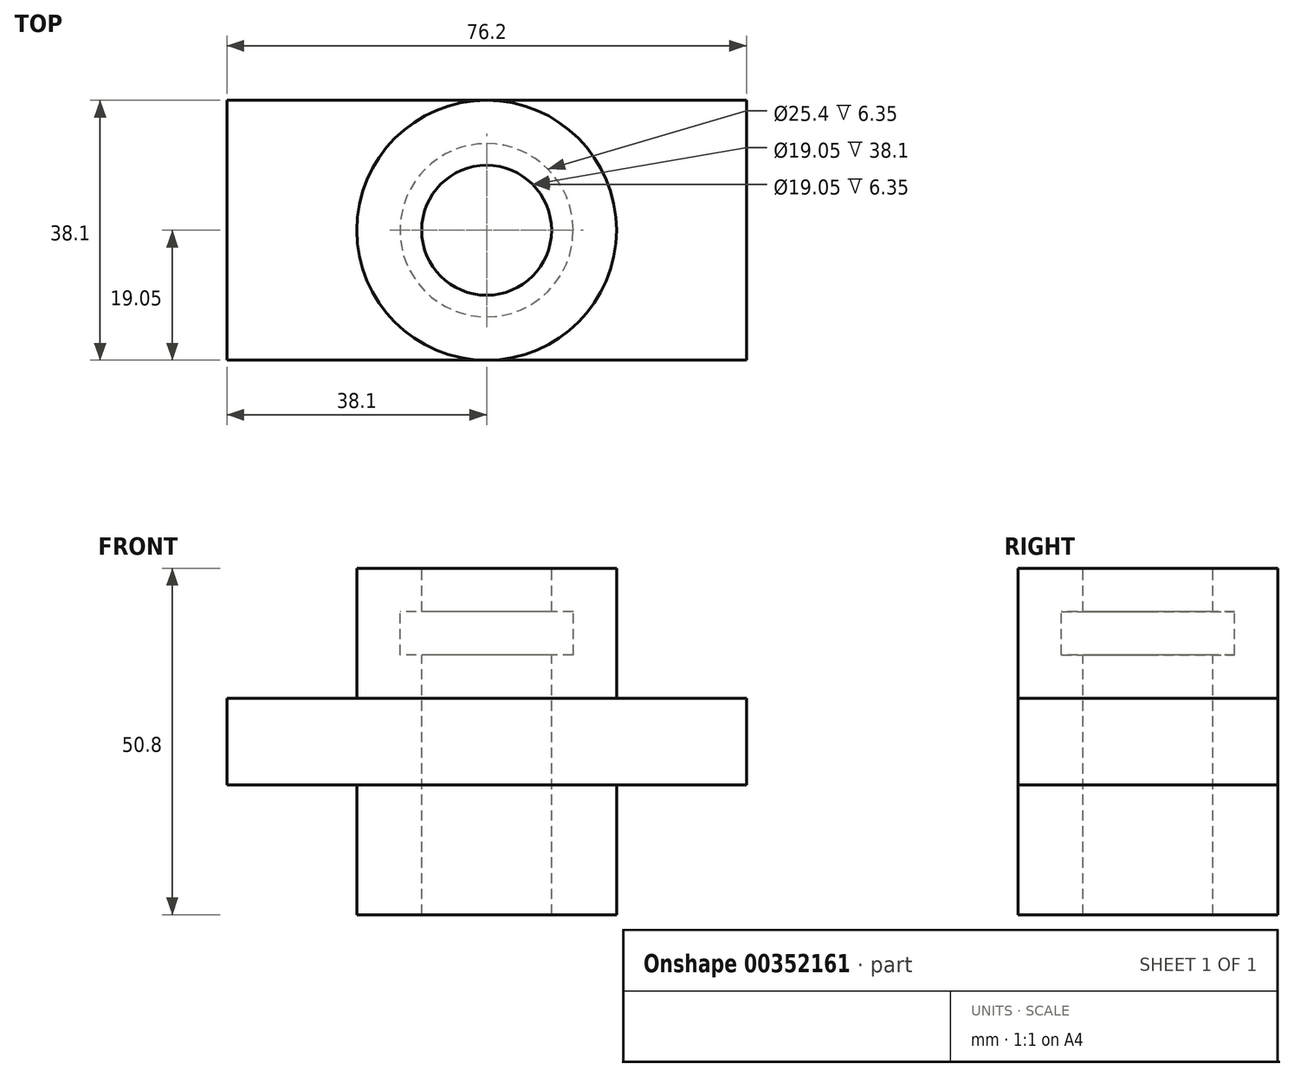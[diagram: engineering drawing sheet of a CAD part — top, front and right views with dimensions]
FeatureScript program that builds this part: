
annotation { "Feature Type Name" : "Feature", "Feature Type Description" : "" }
export const myFeature = defineFeature(function(context is Context, id is Id, definition is map)
    precondition{}
    {
        {
            var Q0;
            Q0=qCreatedBy(makeId("Top.planeOp"),FACE);
            var sketch = newSketch(context, id + "F0", { "sketchPlane" : qUnion([Q0])});
            skLineSegment(sketch, "E0", {"start": v(0, 0) * mm, "end": v(76.2, 0) * mm});
            skLineSegment(sketch, "E1", {"start": v(76.2, 0) * mm, "end": v(76.2, 38.1) * mm});
            skLineSegment(sketch, "E2", {"start": v(76.2, 38.1) * mm, "end": v(0, 38.1) * mm});
            skLineSegment(sketch, "E3", {"start": v(0, 38.1) * mm, "end": v(0, 0) * mm});
            skSolve(sketch);
        }
        {
            var Q0;
            Q0 = qSketchRegion(id + "F0", true);
            extrude(context, id + "F1", {"entities" : qUnion([Q0]), "endBound" : BoundingType.SYMMETRIC, "depth" : 12.7 * mm});
        }
        {
            var Q0;
            Q0=qCreatedBy(makeId("Top.planeOp"),FACE);
            var sketch = newSketch(context, id + "F2", { "sketchPlane" : qUnion([Q0])});
            skCircle(sketch, "E4", {"center": v(38.1, 19.05) * mm, "radius": 19.05 * mm});
            skSolve(sketch);
        }
        {
            var Q0;
            Q0 = qSketchRegion(id + "F2", true);
            extrude(context, id + "F3", {"entities" : qUnion([Q0]), "operationType" : NewBodyOperationType.ADD, "endBound" : BoundingType.SYMMETRIC, "depth" : 50.8 * mm});
        }
        {
            var Q0;
            Q0=makeQuery(id+"F3.opExtrude","CAP_FACE",FACE,{"disambiguationData":[OSD([sQuery(id+"F2.wireOp",EDGE,"E4")])],"isStart":false});
            var sketch = newSketch(context, id + "F4", { "sketchPlane" : qUnion([Q0])});
            skCircle(sketch, "E5", {"center": v(38.1, 19.05) * mm, "radius": 9.53 * mm});
            skSolve(sketch);
        }
        {
            var Q0;
            Q0 = qSketchRegion(id + "F4", true);
            extrude(context, id + "F5", {"entities" : qUnion([Q0]), "operationType" : NewBodyOperationType.REMOVE, "endBound" : BoundingType.THROUGH_ALL, "oppositeDirection" : true, "depth" : 25.4 * mm});
        }
        {
            var Q0;
            Q0=makeQuery(id+"F3.opExtrude","CAP_FACE",FACE,{"disambiguationData":[OSD([sQuery(id+"F2.wireOp",EDGE,"E4")])],"isStart":false});
            var sketch = newSketch(context, id + "F6", { "sketchPlane" : qUnion([Q0])});
            skCircle(sketch, "E6", {"center": v(38.1, 19.05) * mm, "radius": 12.7 * mm});
            skSolve(sketch);
        }
        {
            var Q0;
            Q0=makeQuery(id+"F6.imprint","IMPRINT",FACE,{"disambiguationData":[TD([[makeQuery(id+"F6.imprint","IMPRINT",EDGE,{"derivedFrom":sQuery(id+"F6.wireOp",EDGE,"E6")}),1.0]])]});
            extrude(context, id + "F7", {"entities" : qUnion([Q0]), "operationType" : NewBodyOperationType.REMOVE, "oppositeDirection" : true, "depth" : 12.7 * mm});
        }
        {
            var Q0;
            Q0=makeQuery(id+"F3.opExtrude","CAP_FACE",FACE,{"disambiguationData":[OSD([sQuery(id+"F2.wireOp",EDGE,"E4")])],"isStart":false});
            var sketch = newSketch(context, id + "F8", { "sketchPlane" : qUnion([Q0])});
            skCircle(sketch, "E7", {"center": v(38.1, 19.05) * mm, "radius": 12.7 * mm});
            skSolve(sketch);
        }
        {
            var Q0;
            Q0 = qSketchRegion(id + "F8", true);
            extrude(context, id + "F9", {"entities" : qUnion([Q0]), "operationType" : NewBodyOperationType.ADD, "oppositeDirection" : true, "depth" : 6.35 * mm});
        }
        {
            var Q0;
            Q0=makeQuery(id+"F9.boolean.opBoolean","MERGE",FACE,{"derivedFrom":[makeQuery(id+"F3.opExtrude","CAP_FACE",FACE,{"disambiguationData":[OSD([sQuery(id+"F2.wireOp",EDGE,"E4")])],"isStart":false}),makeQuery(id+"F9.opExtrude","CAP_FACE",FACE,{"disambiguationData":[OSD([sQuery(id+"F8.wireOp",EDGE,"E7")])],"isStart":true})]});
            var sketch = newSketch(context, id + "F10", { "sketchPlane" : qUnion([Q0])});
            skCircle(sketch, "E8", {"center": v(38.1, 19.05) * mm, "radius": 9.53 * mm});
            skSolve(sketch);
        }
        {
            var Q0;
            Q0 = qSketchRegion(id + "F10", true);
            extrude(context, id + "F11", {"entities" : qUnion([Q0]), "operationType" : NewBodyOperationType.REMOVE, "endBound" : BoundingType.THROUGH_ALL, "oppositeDirection" : true, "depth" : 25.4 * mm});
        }
    });
